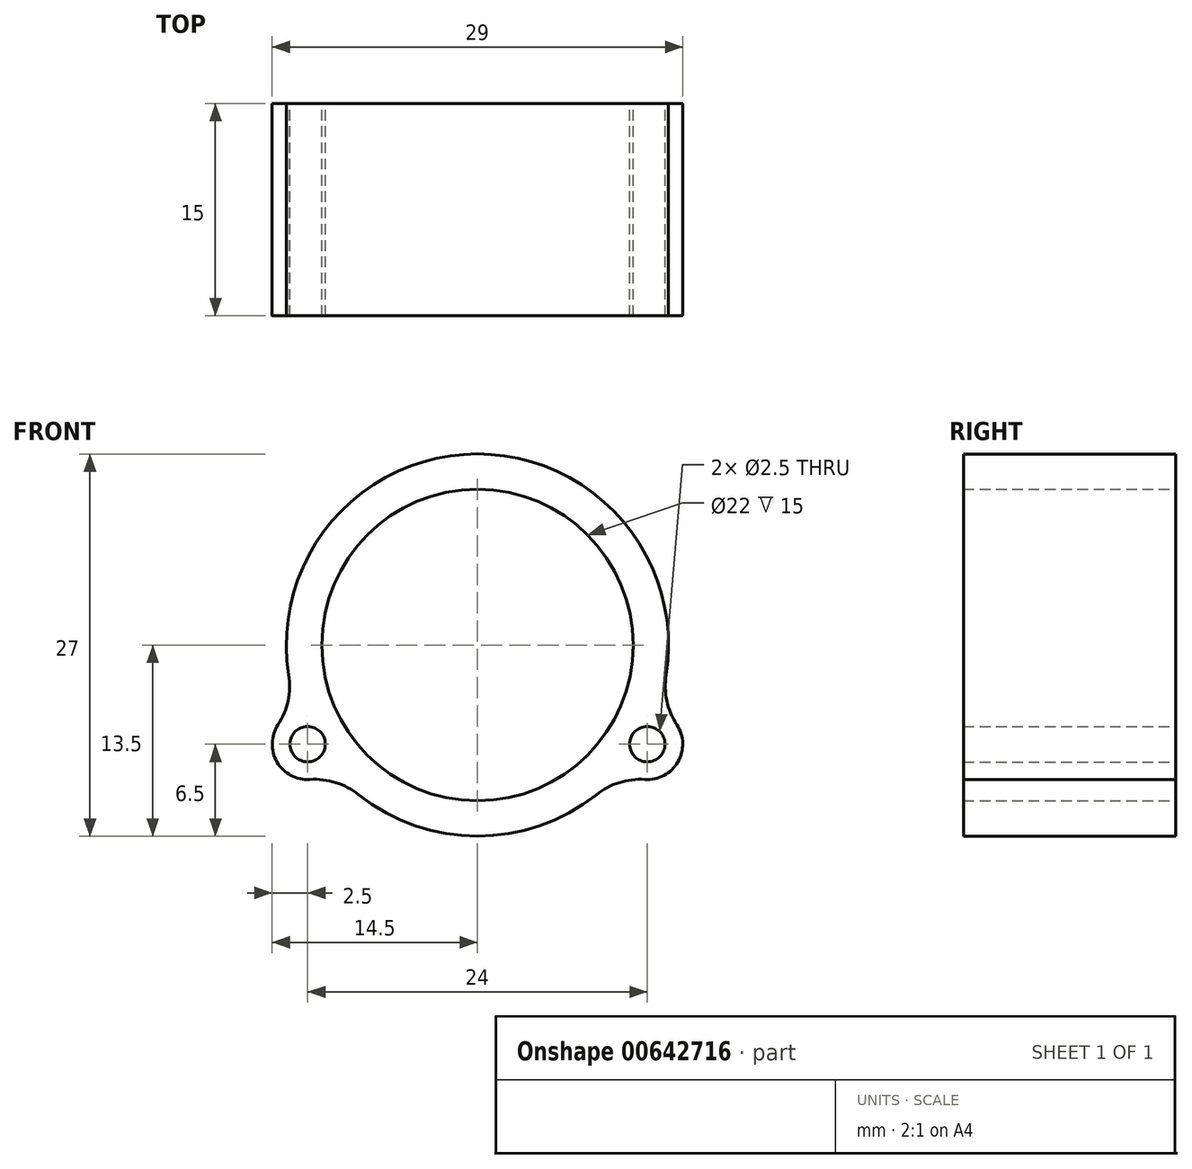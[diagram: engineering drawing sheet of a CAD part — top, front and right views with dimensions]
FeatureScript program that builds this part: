
annotation { "Feature Type Name" : "Feature", "Feature Type Description" : "" }
export const myFeature = defineFeature(function(context is Context, id is Id, definition is map)
    precondition{}
    {
        {
            var Q0;
            Q0=qCreatedBy(makeId("Front.planeOp"),FACE);
            var sketch = newSketch(context, id + "F0", { "sketchPlane" : qUnion([Q0])});
            skCircle(sketch, "E0", {"center": v(0, 0) * mm, "radius": 11 * mm});
            skPoint(sketch, "E1.orphan", {"position": v(11, -7) * mm});
            skPoint(sketch, "E2.orphan", {"position": v(-12.24, -4.39) * mm});
            skPoint(sketch, "E3.start.orphan", {"position": v(-8.49, -7) * mm});
            skCircle(sketch, "E4", {"center": v(-12, -7) * mm, "radius": 1.25 * mm});
            skCircle(sketch, "E5", {"center": v(12, -7) * mm, "radius": 1.25 * mm});
            skPoint(sketch, "E6.visualSharp", {"position": v(13.18, -3) * mm});
            skPoint(sketch, "E7.visualSharp", {"position": v(11.8, -7.54) * mm});
            skPoint(sketch, "E8.visualSharp", {"position": v(-12.65, -3.07) * mm});
            skPoint(sketch, "E9.visualSharp", {"position": v(-11.43, -7.23) * mm});
            skArc(sketch, "E10", {"start": v(-8.4, -10.57) * mm, "mid": v(0, -13.5) * mm, "end": v(8.4, -10.57) * mm});
            skArc(sketch, "E11", {"start": v(-14.1, -5.63) * mm, "mid": v(-14.16, -8.26) * mm, "end": v(-11.84, -9.5) * mm});
            skArc(sketch, "E12", {"start": v(11.84, -9.5) * mm, "mid": v(14.16, -8.26) * mm, "end": v(14.1, -5.63) * mm});
            skArc(sketch, "E13.trimOffspring", {"start": v(13.33, -2.1) * mm, "mid": v(0, 13.5) * mm, "end": v(-13.33, -2.1) * mm});
            skPoint(sketch, "E14.visualSharp", {"position": v(-12.7, -4.6) * mm});
            skArc(sketch, "E14.filletArc", {"start": v(-14.1, -5.63) * mm, "mid": v(-13.38, -3.94) * mm, "end": v(-13.33, -2.1) * mm});
            skPoint(sketch, "E15.visualSharp", {"position": v(-10.25, -8.79) * mm});
            skArc(sketch, "E15.filletArc", {"start": v(-8.4, -10.57) * mm, "mid": v(-10.02, -9.71) * mm, "end": v(-11.84, -9.5) * mm});
            skPoint(sketch, "E16.visualSharp", {"position": v(10.25, -8.79) * mm});
            skArc(sketch, "E16.filletArc", {"start": v(11.84, -9.5) * mm, "mid": v(10.02, -9.71) * mm, "end": v(8.4, -10.57) * mm});
            skPoint(sketch, "E17.visualSharp", {"position": v(12.7, -4.6) * mm});
            skArc(sketch, "E17.filletArc", {"start": v(13.33, -2.1) * mm, "mid": v(13.38, -3.94) * mm, "end": v(14.1, -5.63) * mm});
            skSolve(sketch);
        }
        {
            var Q0;
            Q0=makeQuery(id+"F0.imprint","IMPRINT",FACE,{"disambiguationData":[TD([[makeQuery(id+"F0.imprint","IMPRINT",EDGE,{"derivedFrom":sQuery(id+"F0.wireOp",EDGE,"E0")}),-1.0]])]});
            extrude(context, id + "F1", {"entities" : qUnion([Q0]), "depth" : 15 * mm, "offsetDistance" : 25 * mm});
        }
    });
